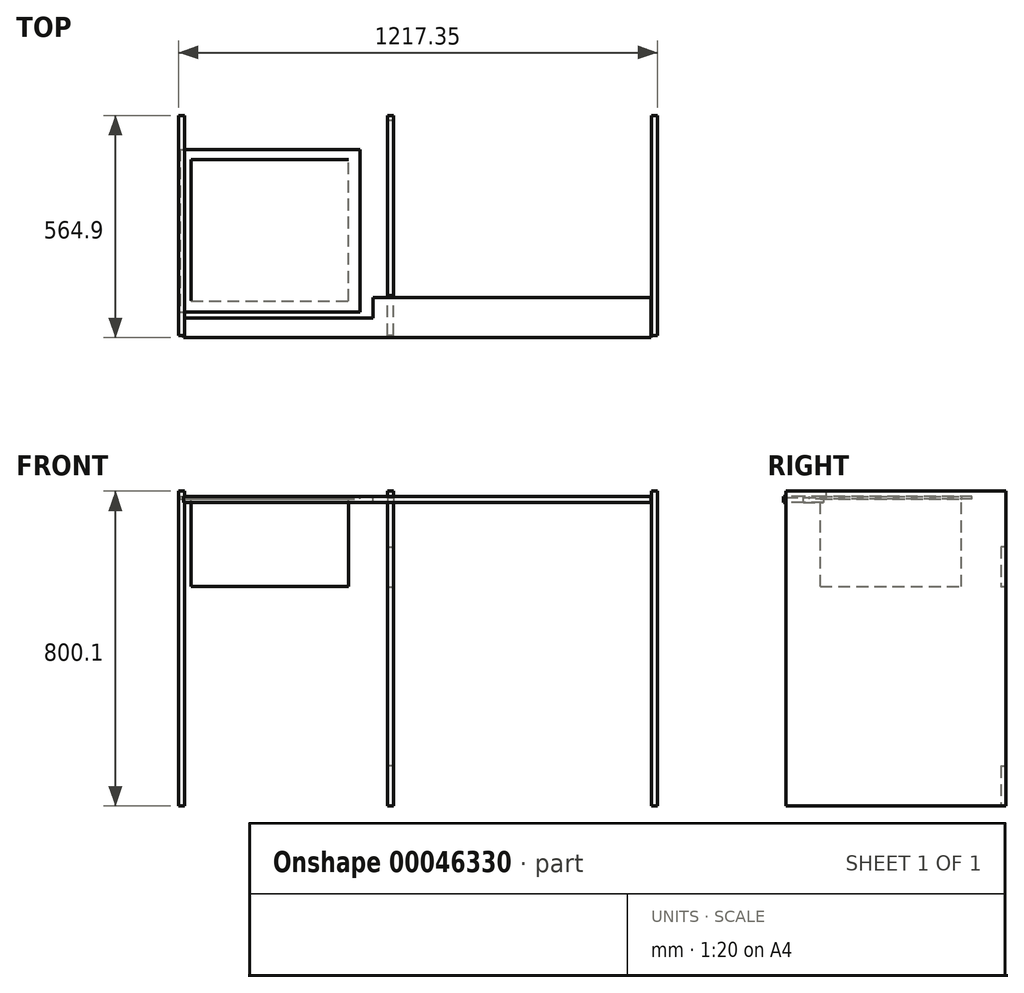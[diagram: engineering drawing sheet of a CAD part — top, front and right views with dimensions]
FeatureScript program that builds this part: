
annotation { "Feature Type Name" : "Feature", "Feature Type Description" : "" }
export const myFeature = defineFeature(function(context is Context, id is Id, definition is map)
    precondition{}
    {
        {
            var Q0;
            Q0=qCreatedBy(makeId("Right.planeOp"),FACE);
            var sketch = newSketch(context, id + "F0", { "sketchPlane" : qUnion([Q0])});
            skLineSegment(sketch, "E0.bottom", {"start": v(-286, 465.2) * mm, "end": v(272.8, 465.2) * mm});
            skLineSegment(sketch, "E0.top", {"start": v(-286, -334.9) * mm, "end": v(272.8, -334.9) * mm});
            skLineSegment(sketch, "E0.left", {"start": v(-286, 465.2) * mm, "end": v(-286, -334.9) * mm});
            skLineSegment(sketch, "E0.right", {"start": v(272.8, 465.2) * mm, "end": v(272.8, -334.9) * mm});
            skSolve(sketch);
        }
        {
            var Q0;
            Q0=makeQuery(id+"F0.imprint","IMPRINT",FACE,{"disambiguationData":[TD([[makeQuery(id+"F0.imprint","IMPRINT",EDGE,{"derivedFrom":sQuery(id+"F0.wireOp",EDGE,"E0.bottom")}),-1.0]])]});
            extrude(context, id + "F1", {"entities" : qUnion([Q0]), "depth" : 15.88 * mm});
        }
        {
            var Q0;
            Q0=makeQuery(id+"F1.opExtrude","SWEPT_BODY",BODY,{"disambiguationData":[OSD([sQuery(id+"F0.wireOp",EDGE,"E0.bottom"),sQuery(id+"F0.wireOp",EDGE,"E0.top"),sQuery(id+"F0.wireOp",EDGE,"E0.left"),sQuery(id+"F0.wireOp",EDGE,"E0.right")])]});
            transform(context, id + "F2", {"entities" : qUnion([Q0]), "transformType" : TransformType.TRANSLATION_3D, "dx" : 1219.2 * mm, "dy" : 0 * mm, "dz" : 0 * mm, "makeCopy" : true});
        }
        {
            var Q0;
            Q0=makeQuery(id+"F1.opExtrude","SWEPT_BODY",BODY,{"disambiguationData":[OSD([sQuery(id+"F0.wireOp",EDGE,"E0.bottom"),sQuery(id+"F0.wireOp",EDGE,"E0.top"),sQuery(id+"F0.wireOp",EDGE,"E0.left"),sQuery(id+"F0.wireOp",EDGE,"E0.right")])]});
            transform(context, id + "F3", {"entities" : qUnion([Q0]), "transformType" : TransformType.TRANSLATION_3D, "dx" : 508 * mm, "dy" : 0 * mm, "dz" : 0 * mm, "makeCopy" : true});
        }
        {
            var Q0;
            Q0=makeQuery(id+"F3.opPattern","COPY",FACE,{"derivedFrom":makeQuery(id+"F1.opExtrude","CAP_FACE",FACE,{"disambiguationData":[OSD([sQuery(id+"F0.wireOp",EDGE,"E0.bottom"),sQuery(id+"F0.wireOp",EDGE,"E0.top"),sQuery(id+"F0.wireOp",EDGE,"E0.left"),sQuery(id+"F0.wireOp",EDGE,"E0.right")])],"isStart":false}),"instanceName":"1"});
            var sketch = newSketch(context, id + "F4", { "sketchPlane" : qUnion([Q0])});
            skLineSegment(sketch, "E1.bottom", {"start": v(-286, 465.2) * mm, "end": v(-184.4, 465.2) * mm});
            skLineSegment(sketch, "E1.top", {"start": v(-286, 449.33) * mm, "end": v(-184.4, 449.33) * mm});
            skLineSegment(sketch, "E1.left", {"start": v(-286, 465.2) * mm, "end": v(-286, 449.33) * mm});
            skLineSegment(sketch, "E1.right", {"start": v(-184.4, 465.2) * mm, "end": v(-184.4, 449.33) * mm});
            skSolve(sketch);
        }
        {
            var Q0;
            Q0 = qSketchRegion(id + "F4", true);
            extrude(context, id + "F5", {"entities" : qUnion([Q0]), "operationType" : NewBodyOperationType.REMOVE, "endBound" : BoundingType.SYMMETRIC, "oppositeDirection" : true, "depth" : 50.8 * mm});
        }
        {
            var Q0;
            Q0=qCreatedBy(makeId("Front.planeOp"),FACE);
            var sketch = newSketch(context, id + "F6", { "sketchPlane" : qUnion([Q0])});
            skLineSegment(sketch, "E2.bottom", {"start": v(15.8, 452.23) * mm, "end": v(1203.26, 452.23) * mm});
            skLineSegment(sketch, "E2.top", {"start": v(15.8, 436.36) * mm, "end": v(1203.26, 436.36) * mm});
            skLineSegment(sketch, "E2.left", {"start": v(15.8, 452.23) * mm, "end": v(15.8, 436.36) * mm});
            skLineSegment(sketch, "E2.right", {"start": v(1203.26, 452.23) * mm, "end": v(1203.26, 436.36) * mm});
            skSolve(sketch);
        }
        {
            var Q0;
            Q0 = qSketchRegion(id + "F6", true);
            extrude(context, id + "F7", {"entities" : qUnion([Q0]), "oppositeDirection" : true, "depth" : 101.6 * mm});
        }
        {
            var Q0;
            Q0=makeQuery(id+"F7.opExtrude","SWEPT_BODY",BODY,{"disambiguationData":[OSD([sQuery(id+"F6.wireOp",EDGE,"E2.bottom"),sQuery(id+"F6.wireOp",EDGE,"E2.top"),sQuery(id+"F6.wireOp",EDGE,"E2.left"),sQuery(id+"F6.wireOp",EDGE,"E2.right")])]});
            transform(context, id + "F8", {"entities" : qUnion([Q0]), "transformType" : TransformType.TRANSLATION_3D, "dx" : 10.16 * mm, "dy" : -292.1 * mm, "dz" : 0 * mm, "makeCopy" : false});
        }
        {
            var Q0;
            Q0=makeQuery(id+"F3.opPattern","COPY",FACE,{"derivedFrom":makeQuery(id+"F1.opExtrude","CAP_FACE",FACE,{"disambiguationData":[OSD([sQuery(id+"F0.wireOp",EDGE,"E0.bottom"),sQuery(id+"F0.wireOp",EDGE,"E0.top"),sQuery(id+"F0.wireOp",EDGE,"E0.left"),sQuery(id+"F0.wireOp",EDGE,"E0.right")])],"isStart":false}),"instanceName":"1"});
            var sketch = newSketch(context, id + "F9", { "sketchPlane" : qUnion([Q0])});
            skLineSegment(sketch, "E3.bottom", {"start": v(272.8, -334.9) * mm, "end": v(260.1, -334.9) * mm});
            skLineSegment(sketch, "E3.top", {"start": v(272.8, -233.3) * mm, "end": v(260.1, -233.3) * mm});
            skLineSegment(sketch, "E3.left", {"start": v(272.8, -334.9) * mm, "end": v(272.8, -233.3) * mm});
            skLineSegment(sketch, "E3.right", {"start": v(260.1, -334.9) * mm, "end": v(260.1, -233.3) * mm});
            skSolve(sketch);
        }
        {
            var Q0;
            Q0 = qSketchRegion(id + "F9", true);
            extrude(context, id + "F10", {"entities" : qUnion([Q0]), "operationType" : NewBodyOperationType.REMOVE, "endBound" : BoundingType.SYMMETRIC, "depth" : 39.37 * mm});
        }
        {
            var Q0;
            Q0=makeQuery(id+"F3.opPattern","COPY",FACE,{"derivedFrom":makeQuery(id+"F1.opExtrude","CAP_FACE",FACE,{"disambiguationData":[OSD([sQuery(id+"F0.wireOp",EDGE,"E0.bottom"),sQuery(id+"F0.wireOp",EDGE,"E0.top"),sQuery(id+"F0.wireOp",EDGE,"E0.left"),sQuery(id+"F0.wireOp",EDGE,"E0.right")])],"isStart":false}),"instanceName":"1"});
            var sketch = newSketch(context, id + "F11", { "sketchPlane" : qUnion([Q0])});
            skLineSegment(sketch, "E4.bottom", {"start": v(272.8, 323.93) * mm, "end": v(260.1, 323.93) * mm});
            skLineSegment(sketch, "E4.top", {"start": v(272.8, 222.33) * mm, "end": v(260.1, 222.33) * mm});
            skLineSegment(sketch, "E4.left", {"start": v(272.8, 323.93) * mm, "end": v(272.8, 222.33) * mm});
            skLineSegment(sketch, "E4.right", {"start": v(260.1, 323.93) * mm, "end": v(260.1, 222.33) * mm});
            skSolve(sketch);
        }
        {
            var Q0;
            Q0 = qSketchRegion(id + "F11", true);
            extrude(context, id + "F12", {"entities" : qUnion([Q0]), "operationType" : NewBodyOperationType.REMOVE, "endBound" : BoundingType.SYMMETRIC, "oppositeDirection" : true, "depth" : 38.1 * mm});
        }
        {
            var Q0;
            Q0=makeQuery(id+"F7.opExtrude","SWEPT_FACE",FACE,{"disambiguationData":[OSD([sQuery(id+"F6.wireOp",EDGE,"E2.bottom")])]});
            var sketch = newSketch(context, id + "F13", { "sketchPlane" : qUnion([Q0])});
            skLineSegment(sketch, "E5.bottom", {"start": v(25.97, -190.5) * mm, "end": v(506.77, -190.5) * mm});
            skLineSegment(sketch, "E5.top", {"start": v(25.97, -241.9) * mm, "end": v(506.77, -241.9) * mm});
            skLineSegment(sketch, "E5.left", {"start": v(25.97, -190.5) * mm, "end": v(25.97, -241.9) * mm});
            skLineSegment(sketch, "E5.right", {"start": v(506.77, -190.5) * mm, "end": v(506.77, -241.9) * mm});
            skSolve(sketch);
        }
        {
            var Q0;
            Q0 = qSketchRegion(id + "F13", true);
            extrude(context, id + "F14", {"entities" : qUnion([Q0]), "operationType" : NewBodyOperationType.REMOVE, "endBound" : BoundingType.THROUGH_ALL, "oppositeDirection" : true, "depth" : 76.2 * mm});
        }
        {
            var Q0;
            Q0=qCreatedBy(makeId("Top.planeOp"),FACE);
            var sketch = newSketch(context, id + "F15", { "sketchPlane" : qUnion([Q0])});
            skLineSegment(sketch, "E6.bottom", {"start": v(70.6, 229.05) * mm, "end": v(527.8, 229.05) * mm});
            skLineSegment(sketch, "E6.top", {"start": v(70.6, -183.7) * mm, "end": v(527.8, -183.7) * mm});
            skLineSegment(sketch, "E6.left", {"start": v(70.6, 229.05) * mm, "end": v(70.6, -183.7) * mm});
            skLineSegment(sketch, "E6.right", {"start": v(527.8, 229.05) * mm, "end": v(527.8, -183.7) * mm});
            skLineSegment(sketch, "E7.bottom", {"start": v(98.45, -155.36) * mm, "end": v(498.5, -155.36) * mm});
            skLineSegment(sketch, "E7.top", {"start": v(98.45, 203.42) * mm, "end": v(498.5, 203.42) * mm});
            skLineSegment(sketch, "E7.left", {"start": v(98.45, -155.36) * mm, "end": v(98.45, 203.42) * mm});
            skLineSegment(sketch, "E7.right", {"start": v(498.5, -155.36) * mm, "end": v(498.5, 203.42) * mm});
            skSolve(sketch);
        }
        {
            var Q0;
            Q0 = qSketchRegion(id + "F15", true);
            extrude(context, id + "F16", {"entities" : qUnion([Q0]), "oppositeDirection" : true, "depth" : 6.35 * mm});
        }
        {
            var Q0;
            Q0=makeQuery(id+"F15.imprint","IMPRINT",FACE,{"disambiguationData":[TD([[makeQuery(id+"F15.imprint","IMPRINT",EDGE,{"derivedFrom":sQuery(id+"F15.wireOp",EDGE,"E7.bottom")}),1.0]])]});
            var sketch = newSketch(context, id + "F17", { "sketchPlane" : qUnion([Q0])});
            skLineSegment(sketch, "E8.bottom", {"start": v(99.2, -156.19) * mm, "end": v(499.24, -156.19) * mm});
            skLineSegment(sketch, "E8.top", {"start": v(99.2, 202.59) * mm, "end": v(499.24, 202.59) * mm});
            skLineSegment(sketch, "E8.left", {"start": v(99.2, -156.19) * mm, "end": v(99.2, 202.59) * mm});
            skLineSegment(sketch, "E8.right", {"start": v(499.24, -156.19) * mm, "end": v(499.24, 202.59) * mm});
            skSolve(sketch);
        }
        {
            var Q0;
            Q0 = qSketchRegion(id + "F17", true);
            extrude(context, id + "F18", {"entities" : qUnion([Q0]), "operationType" : NewBodyOperationType.ADD, "oppositeDirection" : true, "depth" : 228.6 * mm});
        }
        {
            var Q0;
            Q0=makeQuery(id+"F16.opExtrude","SWEPT_BODY",BODY,{"disambiguationData":[OSD([sQuery(id+"F15.wireOp",EDGE,"E6.bottom"),sQuery(id+"F15.wireOp",EDGE,"E6.top"),sQuery(id+"F15.wireOp",EDGE,"E6.left"),sQuery(id+"F15.wireOp",EDGE,"E6.right"),sQuery(id+"F15.wireOp",EDGE,"E7.bottom"),sQuery(id+"F15.wireOp",EDGE,"E7.top"),sQuery(id+"F15.wireOp",EDGE,"E7.left"),sQuery(id+"F15.wireOp",EDGE,"E7.right")])]});
            transform(context, id + "F19", {"entities" : qUnion([Q0]), "transformType" : TransformType.TRANSLATION_3D, "dx" : 0 * mm, "dy" : 0 * mm, "dz" : 451.4 * mm, "makeCopy" : false});
        }
        {
            var Q0;
            Q0=makeQuery(id+"F16.opExtrude","SWEPT_BODY",BODY,{"disambiguationData":[OSD([sQuery(id+"F15.wireOp",EDGE,"E6.bottom"),sQuery(id+"F15.wireOp",EDGE,"E6.top"),sQuery(id+"F15.wireOp",EDGE,"E6.left"),sQuery(id+"F15.wireOp",EDGE,"E6.right"),sQuery(id+"F15.wireOp",EDGE,"E7.bottom"),sQuery(id+"F15.wireOp",EDGE,"E7.top"),sQuery(id+"F15.wireOp",EDGE,"E7.left"),sQuery(id+"F15.wireOp",EDGE,"E7.right")])]});
            transform(context, id + "F20", {"entities" : qUnion([Q0]), "transformType" : TransformType.TRANSLATION_3D, "dx" : -39.77 * mm, "dy" : 0 * mm, "dz" : 0 * mm, "makeCopy" : false});
        }
        {
            var Q0;
            Q0=makeQuery(id+"F16.opExtrude","SWEPT_BODY",BODY,{"disambiguationData":[OSD([sQuery(id+"F15.wireOp",EDGE,"E6.bottom"),sQuery(id+"F15.wireOp",EDGE,"E6.top"),sQuery(id+"F15.wireOp",EDGE,"E6.left"),sQuery(id+"F15.wireOp",EDGE,"E6.right"),sQuery(id+"F15.wireOp",EDGE,"E7.bottom"),sQuery(id+"F15.wireOp",EDGE,"E7.top"),sQuery(id+"F15.wireOp",EDGE,"E7.left"),sQuery(id+"F15.wireOp",EDGE,"E7.right")])]});
            transform(context, id + "F21", {"entities" : qUnion([Q0]), "transformType" : TransformType.TRANSLATION_3D, "dx" : 0 * mm, "dy" : -42.5 * mm, "dz" : 0 * mm, "makeCopy" : false});
        }
        {
            var Q0;
            Q0=makeQuery(id+"F3.opPattern","COPY",BODY,{"derivedFrom":makeQuery(id+"F1.opExtrude","SWEPT_BODY",BODY,{"disambiguationData":[OSD([sQuery(id+"F0.wireOp",EDGE,"E0.bottom"),sQuery(id+"F0.wireOp",EDGE,"E0.top"),sQuery(id+"F0.wireOp",EDGE,"E0.left"),sQuery(id+"F0.wireOp",EDGE,"E0.right")])]}),"instanceName":"1"});
            transform(context, id + "F22", {"entities" : qUnion([Q0]), "transformType" : TransformType.TRANSLATION_3D, "dx" : 36 * mm, "dy" : 0 * mm, "dz" : 0 * mm, "makeCopy" : false});
        }
        {
            var Q0;
            Q0=makeQuery(id+"F16.opExtrude","SWEPT_BODY",BODY,{"disambiguationData":[OSD([sQuery(id+"F15.wireOp",EDGE,"E6.bottom"),sQuery(id+"F15.wireOp",EDGE,"E6.top"),sQuery(id+"F15.wireOp",EDGE,"E6.left"),sQuery(id+"F15.wireOp",EDGE,"E6.right"),sQuery(id+"F15.wireOp",EDGE,"E7.bottom"),sQuery(id+"F15.wireOp",EDGE,"E7.top"),sQuery(id+"F15.wireOp",EDGE,"E7.left"),sQuery(id+"F15.wireOp",EDGE,"E7.right")])]});
            transform(context, id + "F23", {"entities" : qUnion([Q0]), "transformType" : TransformType.TRANSLATION_3D, "dx" : -14.21 * mm, "dy" : 0 * mm, "dz" : 0 * mm, "makeCopy" : false});
        }
        {
            var Q0;
            Q0=makeQuery(id+"F2.opPattern","COPY",BODY,{"derivedFrom":makeQuery(id+"F1.opExtrude","SWEPT_BODY",BODY,{"disambiguationData":[OSD([sQuery(id+"F0.wireOp",EDGE,"E0.bottom"),sQuery(id+"F0.wireOp",EDGE,"E0.top"),sQuery(id+"F0.wireOp",EDGE,"E0.left"),sQuery(id+"F0.wireOp",EDGE,"E0.right")])]}),"instanceName":"1"});
            transform(context, id + "F24", {"entities" : qUnion([Q0]), "transformType" : TransformType.TRANSLATION_3D, "dx" : -5.1 * mm, "dy" : 0 * mm, "dz" : 0 * mm, "makeCopy" : false});
        }
        {
            var Q0;
            Q0=makeQuery(id+"F1.opExtrude","SWEPT_BODY",BODY,{"disambiguationData":[OSD([sQuery(id+"F0.wireOp",EDGE,"E0.bottom"),sQuery(id+"F0.wireOp",EDGE,"E0.top"),sQuery(id+"F0.wireOp",EDGE,"E0.left"),sQuery(id+"F0.wireOp",EDGE,"E0.right")])]});
            transform(context, id + "F25", {"entities" : qUnion([Q0]), "transformType" : TransformType.TRANSLATION_3D, "dx" : 12.63 * mm, "dy" : 0 * mm, "dz" : 0 * mm, "makeCopy" : false});
        }
    });
